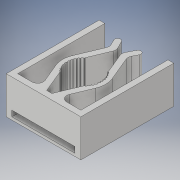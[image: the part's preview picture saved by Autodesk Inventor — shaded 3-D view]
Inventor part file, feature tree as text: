
AUTODESK INVENTOR PART (.ipt)
format: ipt  version: 2019.3 (Build 233278000, 278)  size: 1,111,552 bytes
history: native  units: mm
features: extrude x4, sketch x3, mirror x1, projected_geometry x1
ambient origin geometry x8: Origin, YZ Plane, XZ Plane, XY Plane, X Axis, Y Axis, Z Axis, Center Point
bodies: Body1 (feature_tree)
feature tree (9):
  extrude  "Extrusion2"  Depth=0.5mm
  extrude  "Extrusion4"  Depth=0.5mm
  mirror  "Mirror1"
  extrude  "Extrusion5"  Depth=1.0mm
  extrude  "Extrusion6"  TaperAngle=30.0deg  [1 undecoded]
  sketch  "Sketch2"  dims[d3=5.047545mm d4=0.5mm]
  projected_geometry  "Projected Loop1"
  sketch  "Sketch3"  dims[d5=0.5mm d6=0.5mm]
  sketch  "Sketch4"  dims[d7=60.0deg d8=0.5mm d9=30.0deg d10=400.0mm d12=360.0deg d14=10.0mm d15=0.0mm d16=0.15mm d17=15.0mm d20=22.68928mm d21=2.0mm d22=2.0mm d23=10.0mm d24=10.0mm d25=2.0mm d26=4.0mm d27=2.0mm d28=1.0mm d29=2.0mm d30=2.0mm d31=3.0mm d32=11.0mm d34=10.0mm d35=0.0mm d36=2.0mm d37=0.0mm d38=1.0mm d39=0.0mm]
note: 1 required parameter value undecoded (feature->parameter linkage not recoverable at this tier; creation-order binding heuristic only, values carry confidence <= 0.55)
